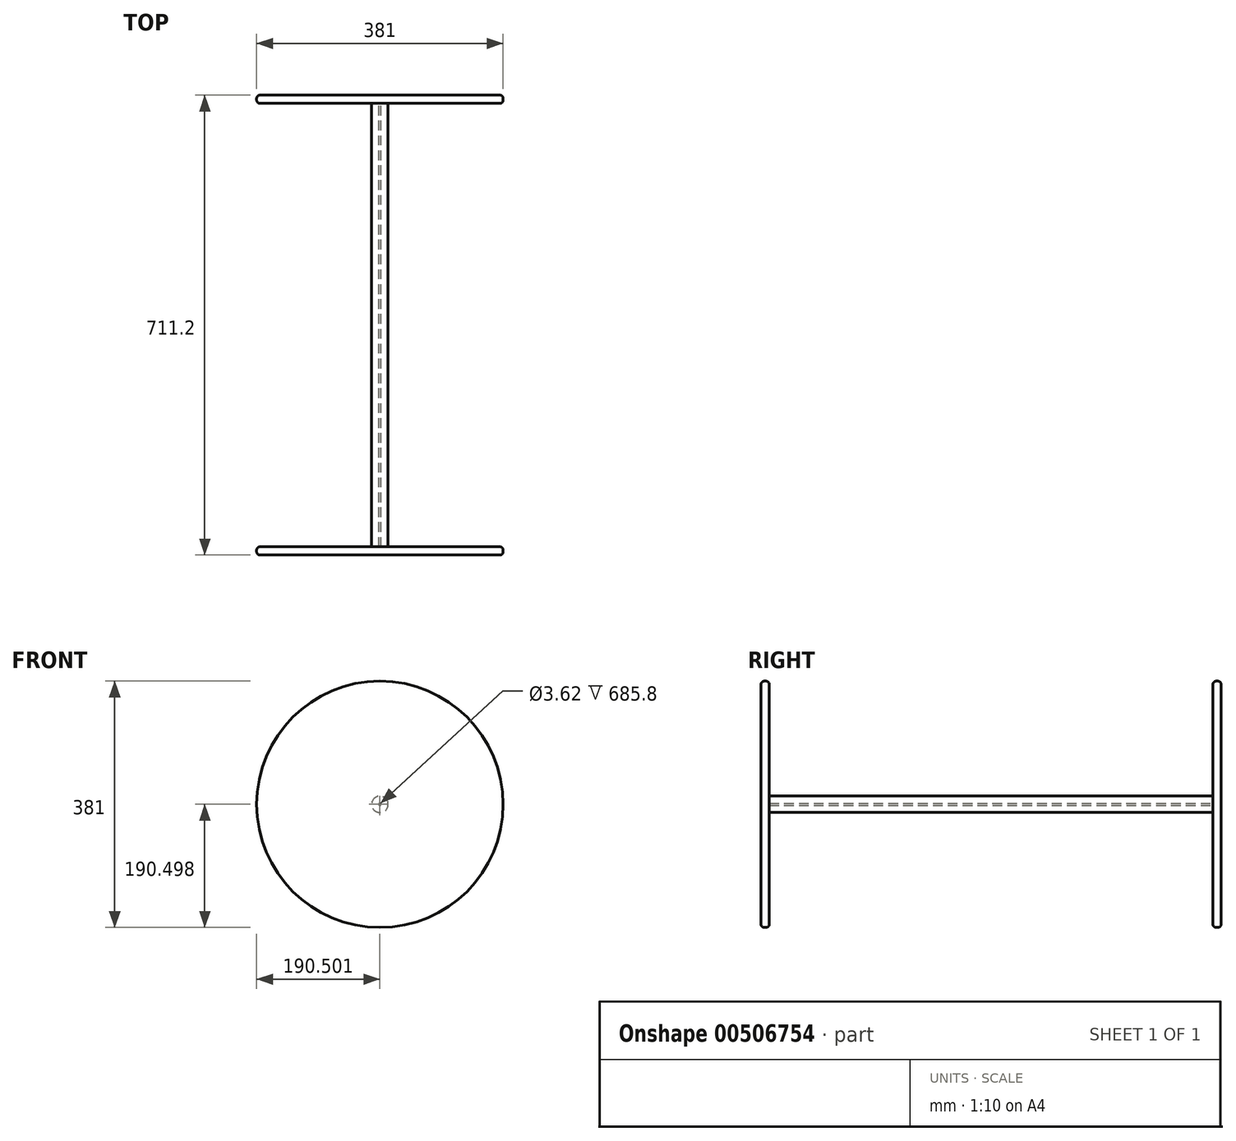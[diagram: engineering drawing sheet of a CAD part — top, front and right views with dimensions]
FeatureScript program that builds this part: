
annotation { "Feature Type Name" : "Feature", "Feature Type Description" : "" }
export const myFeature = defineFeature(function(context is Context, id is Id, definition is map)
    precondition{}
    {
        {
            var Q0;
            Q0=qCreatedBy(makeId("Front.planeOp"),FACE);
            var sketch = newSketch(context, id + "F0", { "sketchPlane" : qUnion([Q0])});
            skCircle(sketch, "E0", {"center": v(-12.77, 10.29) * mm, "radius": 190.5 * mm});
            skSolve(sketch);
        }
        {
            var Q0;
            Q0 = qSketchRegion(id + "F0", true);
            extrude(context, id + "F1", {"entities" : qUnion([Q0]), "depth" : 12.7 * mm});
        }
        {
            var Q0;
            Q0=makeQuery(id+"F1.opExtrude","CAP_FACE",FACE,{"disambiguationData":[OSD([sQuery(id+"F0.wireOp",EDGE,"E0")])],"isStart":false});
            var sketch = newSketch(context, id + "F2", { "sketchPlane" : qUnion([Q0])});
            skCircle(sketch, "E1", {"center": v(-12.77, 10.29) * mm, "radius": 1.8 * mm});
            skCircle(sketch, "E2", {"center": v(-12.77, 10.29) * mm, "radius": 12.7 * mm});
            skSolve(sketch);
        }
        {
            var Q0;
            Q0 = qSketchRegion(id + "F2", true);
            extrude(context, id + "F3", {"entities" : qUnion([Q0]), "operationType" : NewBodyOperationType.ADD, "depth" : 685.8 * mm, "offsetDistance" : 25.4 * mm});
        }
        {
            var Q0;
            Q0=makeQuery(id+"F3.opExtrude","CAP_FACE",FACE,{"disambiguationData":[OSD([sQuery(id+"F2.wireOp",EDGE,"E1")])],"isStart":false});
            var sketch = newSketch(context, id + "F4", { "sketchPlane" : qUnion([Q0])});
            skCircle(sketch, "E3", {"center": v(-12.77, 10.29) * mm, "radius": 190.5 * mm});
            skSolve(sketch);
        }
        {
            var Q0;
            Q0 = qSketchRegion(id + "F4", true);
            extrude(context, id + "F5", {"entities" : qUnion([Q0]), "operationType" : NewBodyOperationType.ADD, "depth" : 12.7 * mm});
        }
        {
            var Q0;
            Q0=makeQuery(id+"F5.opExtrude","CAP_EDGE",EDGE,{"disambiguationData":[OSD([sQuery(id+"F4.wireOp",EDGE,"E3")])],"isStart":false});
            var Q1;
            Q1=makeQuery(id+"F5.opExtrude","CAP_EDGE",EDGE,{"disambiguationData":[OSD([sQuery(id+"F4.wireOp",EDGE,"E3")])],"isStart":true});
            var Q2;
            Q2=makeQuery(id+"F1.opExtrude","CAP_EDGE",EDGE,{"disambiguationData":[OSD([sQuery(id+"F0.wireOp",EDGE,"E0")])],"isStart":false});
            var Q3;
            Q3=makeQuery(id+"F1.opExtrude","CAP_EDGE",EDGE,{"disambiguationData":[OSD([sQuery(id+"F0.wireOp",EDGE,"E0")])],"isStart":true});
            fillet(context, id + "F6", {"entities" : qUnion([Q0, Q1, Q2, Q3]), "radius" : 5.08 * mm, "tangentPropagation" : true, "allowEdgeOverflow" : false});
        }
    });
